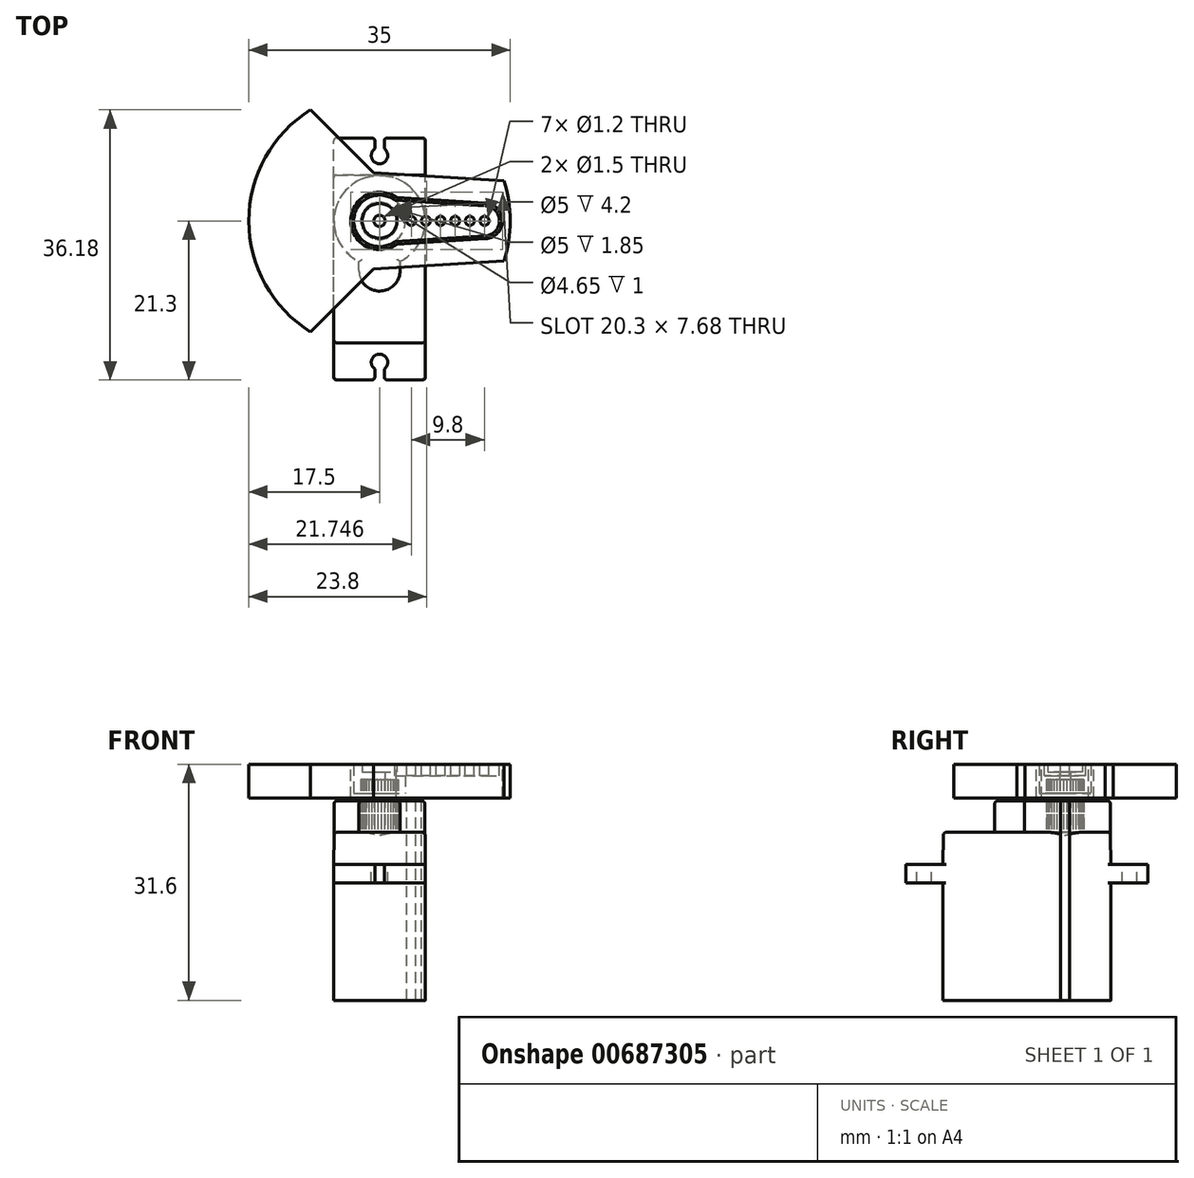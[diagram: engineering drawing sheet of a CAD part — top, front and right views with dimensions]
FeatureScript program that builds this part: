
annotation { "Feature Type Name" : "Feature", "Feature Type Description" : "" }
export const myFeature = defineFeature(function(context is Context, id is Id, definition is map)
    precondition{}
    {
        {
            var Q0;
            Q0=qCreatedBy(makeId("Top.planeOp"),FACE);
            var sketch = newSketch(context, id + "F0", { "sketchPlane" : qUnion([Q0])});
            skLineSegment(sketch, "E0.bottom", {"start": v(6.15, -11.25) * mm, "end": v(-6.15, -11.25) * mm});
            skLineSegment(sketch, "E0.top", {"start": v(6.15, 11.25) * mm, "end": v(-6.15, 11.25) * mm});
            skLineSegment(sketch, "E0.left", {"start": v(6.15, -11.25) * mm, "end": v(6.15, 11.25) * mm});
            skLineSegment(sketch, "E0.right", {"start": v(-6.15, -11.25) * mm, "end": v(-6.15, 11.25) * mm});
            skPoint(sketch, "E0.middle", {"position": v(0, 0) * mm});
            skSolve(sketch);
        }
        {
            var Q0;
            Q0=qSketchRegion(id+"F0",true);
            extrude(context, id + "F1", {"entities" : qUnion([Q0]), "depth" : (22.5 - 15.7) * mm, "hasDraft" : true, "draftAngle" : .5 * degree, "draftPullDirection" : true, "hasSecondDirection" : true, "secondDirectionOppositeDirection" : true, "secondDirectionDepth" : 15.7 * mm});
        }
        {
            var Q0;
            Q0=qCreatedBy(makeId("Top.planeOp"),FACE);
            var sketch = newSketch(context, id + "F2", { "sketchPlane" : qUnion([Q0])});
            skLineSegment(sketch, "E1.bottom", {"start": v(6.15, -16.2) * mm, "end": v(-6.15, -16.2) * mm});
            skLineSegment(sketch, "E1.top", {"start": v(6.15, 16.2) * mm, "end": v(-6.15, 16.2) * mm});
            skLineSegment(sketch, "E1.left", {"start": v(6.15, -16.2) * mm, "end": v(6.15, 16.2) * mm});
            skLineSegment(sketch, "E1.right", {"start": v(-6.15, -16.2) * mm, "end": v(-6.15, 16.2) * mm});
            skPoint(sketch, "E1.middle", {"position": v(0, 0) * mm});
            skSolve(sketch);
        }
        {
            var Q0;
            Q0=qSketchRegion(id+"F2",true);
            extrude(context, id + "F3", {"entities" : qUnion([Q0]), "operationType" : NewBodyOperationType.ADD, "depth" : 2.5 * mm, "hasDraft" : true, "draftAngle" : .5 * degree, "draftPullDirection" : true});
        }
        {
            var Q0;
            {var subQ0=sQuery(id+"F2.wireOp",EDGE,"E1.top");var subQ1=sQuery(id+"F2.wireOp",EDGE,"E1.right");var subQ2=sQuery(id+"F2.wireOp",EDGE,"E1.left");Q0=makeQuery(id+"F3.boolean.opBoolean","SPLIT",FACE,{"disambiguationData":[TD([makeQuery(id+"F1.opExtrude","SWEPT_FACE",FACE,{"disambiguationData":[OSD([sQuery(id+"F0.wireOp",EDGE,"E0.top")])]})])],"derivedFrom":makeQuery(id+"F3.opExtrude","CAP_FACE",FACE,{"disambiguationData":[OSD([sQuery(id+"F2.wireOp",EDGE,"E1.bottom"),subQ0,subQ2,subQ1])],"isStart":false})});}
            var sketch = newSketch(context, id + "F4", { "sketchPlane" : qUnion([Q0])});
            skArc(sketch, "E2", {"start": v(-0.63, 14.76) * mm, "mid": v(0, 12.75) * mm, "end": v(0.63, 14.76) * mm});
            skLineSegment(sketch, "E3", {"start": v(0, 0) * mm, "end": v(0, 13.85) * mm, "construction": true});
            skLineSegment(sketch, "E4", {"start": v(-0.63, 14.76) * mm, "end": v(-0.63, 16.2) * mm});
            skLineSegment(sketch, "E5", {"start": v(-0.62, 16.2) * mm, "end": v(0.62, 16.2) * mm});
            skLineSegment(sketch, "E6", {"start": v(0.62, 16.2) * mm, "end": v(0.62, 14.76) * mm});
            skLineSegment(sketch, "E7", {"start": v(0, 13.85) * mm, "end": v(0, 16.2) * mm, "construction": true});
            skLineSegment(sketch, "E8.MirrorCS", {"start": v(0.62, -16.2) * mm, "end": v(0.62, -14.76) * mm});
            skLineSegment(sketch, "E9.MirrorCS", {"start": v(-0.62, -16.2) * mm, "end": v(0.62, -16.2) * mm});
            skLineSegment(sketch, "E10.MirrorCS", {"start": v(-0.63, -14.76) * mm, "end": v(-0.63, -16.2) * mm});
            skArc(sketch, "E11.MirrorCS", {"start": v(-0.63, -14.76) * mm, "mid": v(0, -12.75) * mm, "end": v(0.63, -14.76) * mm});
            skSolve(sketch);
        }
        {
            var Q0;
            Q0=qSketchRegion(id+"F4",true);
            extrude(context, id + "F5", {"entities" : qUnion([Q0]), "operationType" : NewBodyOperationType.REMOVE, "endBound" : BoundingType.THROUGH_ALL, "oppositeDirection" : true, "depth" : 25 * mm});
        }
        {
            var Q0;
            Q0=makeQuery(id+"F1.*.split.splitOp","SPLIT",EDGE,{"derivedFrom":makeQuery(id+"F1.opExtrude","SWEPT_EDGE",EDGE,{"disambiguationData":[OSD([sQuery(id+"F0.wireOp",EDGE,"E0.bottom"),sQuery(id+"F0.wireOp",EDGE,"E0.left")])]})});
            var Q1;
            Q1=makeQuery(id+"F1.*.split.splitOp","SPLIT",EDGE,{"derivedFrom":makeQuery(id+"F1.opExtrude","SWEPT_EDGE",EDGE,{"disambiguationData":[OSD([sQuery(id+"F0.wireOp",EDGE,"E0.bottom"),sQuery(id+"F0.wireOp",EDGE,"E0.left")])]}),"isFromBackBody":true});
            var Q2;
            Q2=makeQuery(id+"F1.*.split.splitOp","SPLIT",EDGE,{"derivedFrom":makeQuery(id+"F1.opExtrude","SWEPT_EDGE",EDGE,{"disambiguationData":[OSD([sQuery(id+"F0.wireOp",EDGE,"E0.bottom"),sQuery(id+"F0.wireOp",EDGE,"E0.right")])]}),"isFromBackBody":true});
            var Q3;
            Q3=makeQuery(id+"F1.*.split.splitOp","SPLIT",EDGE,{"derivedFrom":makeQuery(id+"F1.opExtrude","SWEPT_EDGE",EDGE,{"disambiguationData":[OSD([sQuery(id+"F0.wireOp",EDGE,"E0.bottom"),sQuery(id+"F0.wireOp",EDGE,"E0.right")])]})});
            var Q4;
            Q4=makeQuery(id+"F1.opExtrude","CAP_FACE",FACE,{"disambiguationData":[OSD([sQuery(id+"F0.wireOp",EDGE,"E0.bottom"),sQuery(id+"F0.wireOp",EDGE,"E0.top"),sQuery(id+"F0.wireOp",EDGE,"E0.left"),sQuery(id+"F0.wireOp",EDGE,"E0.right")])],"isStart":false});
            var Q5;
            Q5=makeQuery(id+"F1.*.split.splitOp","SPLIT",EDGE,{"derivedFrom":makeQuery(id+"F1.opExtrude","SWEPT_EDGE",EDGE,{"disambiguationData":[OSD([sQuery(id+"F0.wireOp",EDGE,"E0.top"),sQuery(id+"F0.wireOp",EDGE,"E0.right")])]})});
            var Q6;
            Q6=makeQuery(id+"F1.*.split.splitOp","SPLIT",EDGE,{"derivedFrom":makeQuery(id+"F1.opExtrude","SWEPT_EDGE",EDGE,{"disambiguationData":[OSD([sQuery(id+"F0.wireOp",EDGE,"E0.top"),sQuery(id+"F0.wireOp",EDGE,"E0.right")])]}),"isFromBackBody":true});
            var Q7;
            Q7=makeQuery(id+"F1.*.split.splitOp","SPLIT",EDGE,{"derivedFrom":makeQuery(id+"F1.opExtrude","SWEPT_EDGE",EDGE,{"disambiguationData":[OSD([sQuery(id+"F0.wireOp",EDGE,"E0.top"),sQuery(id+"F0.wireOp",EDGE,"E0.left")])]}),"isFromBackBody":true});
            var Q8;
            Q8=makeQuery(id+"F1.*.split.splitOp","SPLIT",EDGE,{"derivedFrom":makeQuery(id+"F1.opExtrude","SWEPT_EDGE",EDGE,{"disambiguationData":[OSD([sQuery(id+"F0.wireOp",EDGE,"E0.top"),sQuery(id+"F0.wireOp",EDGE,"E0.left")])]})});
            var Q9;
            Q9=makeQuery(id+"F3.opExtrude","SWEPT_EDGE",EDGE,{"disambiguationData":[OSD([sQuery(id+"F2.wireOp",EDGE,"E1.top"),sQuery(id+"F2.wireOp",EDGE,"E1.left")])]});
            var Q10;
            Q10=makeQuery(id+"F5.boolean.opBoolean","INTERSECT",EDGE,{"derivedFrom":[makeQuery(id+"F3.opExtrude","SWEPT_FACE",FACE,{"disambiguationData":[OSD([sQuery(id+"F2.wireOp",EDGE,"E1.top")])]}),makeQuery(id+"F5.opExtrude","SWEPT_FACE",FACE,{"disambiguationData":[OSD([sQuery(id+"F4.wireOp",EDGE,"E6")])]})]});
            var Q11;
            Q11=makeQuery(id+"F5.boolean.opBoolean","INTERSECT",EDGE,{"derivedFrom":[makeQuery(id+"F3.opExtrude","SWEPT_FACE",FACE,{"disambiguationData":[OSD([sQuery(id+"F2.wireOp",EDGE,"E1.top")])]}),makeQuery(id+"F5.opExtrude","SWEPT_FACE",FACE,{"disambiguationData":[OSD([sQuery(id+"F4.wireOp",EDGE,"E4")])]})]});
            var Q12;
            Q12=makeQuery(id+"F3.opExtrude","SWEPT_EDGE",EDGE,{"disambiguationData":[OSD([sQuery(id+"F2.wireOp",EDGE,"E1.top"),sQuery(id+"F2.wireOp",EDGE,"E1.right")])]});
            var Q13;
            Q13=makeQuery(id+"F3.opExtrude","SWEPT_EDGE",EDGE,{"disambiguationData":[OSD([sQuery(id+"F2.wireOp",EDGE,"E1.bottom"),sQuery(id+"F2.wireOp",EDGE,"E1.right")])]});
            var Q14;
            Q14=makeQuery(id+"F5.boolean.opBoolean","INTERSECT",EDGE,{"derivedFrom":[makeQuery(id+"F3.opExtrude","SWEPT_FACE",FACE,{"disambiguationData":[OSD([sQuery(id+"F2.wireOp",EDGE,"E1.bottom")])]}),makeQuery(id+"F5.opExtrude","SWEPT_FACE",FACE,{"disambiguationData":[OSD([sQuery(id+"F4.wireOp",EDGE,"E10.MirrorCS")])]})]});
            var Q15;
            Q15=makeQuery(id+"F5.boolean.opBoolean","INTERSECT",EDGE,{"derivedFrom":[makeQuery(id+"F3.opExtrude","SWEPT_FACE",FACE,{"disambiguationData":[OSD([sQuery(id+"F2.wireOp",EDGE,"E1.bottom")])]}),makeQuery(id+"F5.opExtrude","SWEPT_FACE",FACE,{"disambiguationData":[OSD([sQuery(id+"F4.wireOp",EDGE,"E8.MirrorCS")])]})]});
            var Q16;
            Q16=makeQuery(id+"F3.opExtrude","SWEPT_EDGE",EDGE,{"disambiguationData":[OSD([sQuery(id+"F2.wireOp",EDGE,"E1.bottom"),sQuery(id+"F2.wireOp",EDGE,"E1.left")])]});
            fillet(context, id + "F6", {"entities" : qUnion([Q0, Q1, Q2, Q3, Q4, Q5, Q6, Q7, Q8, Q9, Q10, Q11, Q12, Q13, Q14, Q15, Q16]), "radius" : .4 * mm, "tangentPropagation" : true, "allowEdgeOverflow" : false});
        }
        {
            var Q0;
            Q0=makeQuery(id+"F1.opExtrude","CAP_FACE",FACE,{"disambiguationData":[OSD([sQuery(id+"F0.wireOp",EDGE,"E0.bottom"),sQuery(id+"F0.wireOp",EDGE,"E0.top"),sQuery(id+"F0.wireOp",EDGE,"E0.left"),sQuery(id+"F0.wireOp",EDGE,"E0.right")])],"isStart":false});
            var sketch = newSketch(context, id + "F7", { "sketchPlane" : qUnion([Q0])});
            skArc(sketch, "E12", {"start": v(2.75, -0.34) * mm, "mid": v(0, 11.2) * mm, "end": v(-2.75, -0.34) * mm});
            skLineSegment(sketch, "E13", {"start": v(-2.75, -0.34) * mm, "end": v(-2.75, -1.56) * mm});
            skLineSegment(sketch, "E14", {"start": v(2.75, -0.34) * mm, "end": v(2.75, -1.56) * mm});
            skArc(sketch, "E15", {"start": v(-2.75, -1.56) * mm, "mid": v(0, -4.3) * mm, "end": v(2.75, -1.56) * mm});
            skCircle(sketch, "E16", {"center": v(0, 5.1) * mm, "radius": 2.5 * mm});
            skSolve(sketch);
        }
        {
            var Q0;
            Q0=qSketchRegion(id+"F7",true);
            extrude(context, id + "F8", {"entities" : qUnion([Q0]), "operationType" : NewBodyOperationType.ADD, "depth" : 4.2 * mm, "hasSecondDirection" : true, "secondDirectionBound" : SecondDirectionBoundingType.UP_TO_NEXT, "secondDirectionOppositeDirection" : true, "secondDirectionDepth" : 25 * mm});
        }
        {
            var Q0;
            Q0=makeQuery(id+"F8.opExtrude","CAP_EDGE",EDGE,{"disambiguationData":[OSD([sQuery(id+"F7.wireOp",EDGE,"E12")])],"isStart":false});
            var Q1;
            Q1=makeQuery(id+"F8.opExtrude","CAP_EDGE",EDGE,{"disambiguationData":[OSD([sQuery(id+"F7.wireOp",EDGE,"E14")])],"isStart":false});
            var Q2;
            Q2=makeQuery(id+"F8.opExtrude","CAP_EDGE",EDGE,{"disambiguationData":[OSD([sQuery(id+"F7.wireOp",EDGE,"E15")])],"isStart":false});
            var Q3;
            Q3=makeQuery(id+"F8.opExtrude","CAP_EDGE",EDGE,{"disambiguationData":[OSD([sQuery(id+"F7.wireOp",EDGE,"E13")])],"isStart":false});
            fillet(context, id + "F9", {"entities" : qUnion([Q0, Q1, Q2, Q3]), "radius" : .4 * mm, "tangentPropagation" : true, "allowEdgeOverflow" : false});
        }
        {
            var Q0;
            Q0=makeQuery(id+"F8.opExtrude","CAP_FACE",FACE,{"disambiguationData":[OSD([sQuery(id+"F7.wireOp",EDGE,"E12"),sQuery(id+"F7.wireOp",EDGE,"E13"),sQuery(id+"F7.wireOp",EDGE,"E14"),sQuery(id+"F7.wireOp",EDGE,"E15"),sQuery(id+"F7.wireOp",EDGE,"E16")])],"isStart":false});
            var sketch = newSketch(context, id + "F10", { "sketchPlane" : qUnion([Q0])});
            skCircle(sketch, "E17", {"center": v(0, 5.1) * mm, "radius": 2.3 * mm, "construction": true});
            skLineSegment(sketch, "E18", {"start": v(-0.23, 7.39) * mm, "end": v(-0.06, 7.57) * mm});
            skLineSegment(sketch, "E19", {"start": v(0.23, 7.39) * mm, "end": v(0.06, 7.57) * mm});
            skArc(sketch, "E20", {"start": v(0.06, 7.57) * mm, "mid": v(0, 7.6) * mm, "end": v(-0.06, 7.57) * mm});
            skLineSegment(sketch, "E21", {"start": v(-0.23, 7.39) * mm, "end": v(0, 5.1) * mm, "construction": true});
            skLineSegment(sketch, "E22", {"start": v(0.23, 7.39) * mm, "end": v(0, 5.1) * mm, "construction": true});
            skLineSegment(sketch, "E23.1.0", {"start": v(-0.67, 7.3) * mm, "end": v(-0.54, 7.51) * mm});
            skArc(sketch, "E23.1.1", {"start": v(-0.42, 7.54) * mm, "mid": v(-0.49, 7.55) * mm, "end": v(-0.54, 7.51) * mm});
            skLineSegment(sketch, "E23.1.2", {"start": v(-0.23, 7.39) * mm, "end": v(-0.42, 7.54) * mm});
            skLineSegment(sketch, "E23.2.0", {"start": v(-1.08, 7.13) * mm, "end": v(-1, 7.36) * mm});
            skArc(sketch, "E23.2.1", {"start": v(-0.9, 7.4) * mm, "mid": v(-0.96, 7.4) * mm, "end": v(-1, 7.36) * mm});
            skLineSegment(sketch, "E23.2.2", {"start": v(-0.67, 7.3) * mm, "end": v(-0.9, 7.4) * mm});
            skLineSegment(sketch, "E23.3.0", {"start": v(-1.46, 6.88) * mm, "end": v(-1.42, 7.12) * mm});
            skArc(sketch, "E23.3.1", {"start": v(-1.32, 7.19) * mm, "mid": v(-1.39, 7.18) * mm, "end": v(-1.42, 7.12) * mm});
            skLineSegment(sketch, "E23.3.2", {"start": v(-1.08, 7.13) * mm, "end": v(-1.32, 7.19) * mm});
            skLineSegment(sketch, "E23.4.0", {"start": v(-1.78, 6.56) * mm, "end": v(-1.8, 6.8) * mm});
            skArc(sketch, "E23.4.1", {"start": v(-1.7, 6.9) * mm, "mid": v(-1.77, 6.87) * mm, "end": v(-1.8, 6.8) * mm});
            skLineSegment(sketch, "E23.4.2", {"start": v(-1.46, 6.88) * mm, "end": v(-1.7, 6.9) * mm});
            skLineSegment(sketch, "E23.5.0", {"start": v(-2.03, 6.18) * mm, "end": v(-2.09, 6.42) * mm});
            skArc(sketch, "E23.5.1", {"start": v(-2.02, 6.52) * mm, "mid": v(-2.08, 6.49) * mm, "end": v(-2.09, 6.42) * mm});
            skLineSegment(sketch, "E23.5.2", {"start": v(-1.78, 6.56) * mm, "end": v(-2.02, 6.52) * mm});
            skLineSegment(sketch, "E23.6.0", {"start": v(-2.2, 5.77) * mm, "end": v(-2.3, 6) * mm});
            skArc(sketch, "E23.6.1", {"start": v(-2.26, 6.1) * mm, "mid": v(-2.3, 6.06) * mm, "end": v(-2.3, 6) * mm});
            skLineSegment(sketch, "E23.6.2", {"start": v(-2.03, 6.18) * mm, "end": v(-2.26, 6.1) * mm});
            skLineSegment(sketch, "E23.7.0", {"start": v(-2.29, 5.33) * mm, "end": v(-2.44, 5.52) * mm});
            skArc(sketch, "E23.7.1", {"start": v(-2.41, 5.64) * mm, "mid": v(-2.45, 5.59) * mm, "end": v(-2.44, 5.52) * mm});
            skLineSegment(sketch, "E23.7.2", {"start": v(-2.2, 5.77) * mm, "end": v(-2.41, 5.64) * mm});
            skLineSegment(sketch, "E23.8.0", {"start": v(-2.29, 4.87) * mm, "end": v(-2.47, 5.04) * mm});
            skArc(sketch, "E23.8.1", {"start": v(-2.47, 5.16) * mm, "mid": v(-2.5, 5.1) * mm, "end": v(-2.47, 5.04) * mm});
            skLineSegment(sketch, "E23.8.2", {"start": v(-2.29, 5.33) * mm, "end": v(-2.47, 5.16) * mm});
            skLineSegment(sketch, "E23.9.0", {"start": v(-2.2, 4.43) * mm, "end": v(-2.41, 4.56) * mm});
            skArc(sketch, "E23.9.1", {"start": v(-2.44, 4.68) * mm, "mid": v(-2.45, 4.61) * mm, "end": v(-2.41, 4.56) * mm});
            skLineSegment(sketch, "E23.9.2", {"start": v(-2.29, 4.87) * mm, "end": v(-2.44, 4.68) * mm});
            skLineSegment(sketch, "E23.10.0", {"start": v(-2.03, 4.02) * mm, "end": v(-2.26, 4.1) * mm});
            skArc(sketch, "E23.10.1", {"start": v(-2.3, 4.2) * mm, "mid": v(-2.3, 4.14) * mm, "end": v(-2.26, 4.1) * mm});
            skLineSegment(sketch, "E23.10.2", {"start": v(-2.2, 4.43) * mm, "end": v(-2.3, 4.2) * mm});
            skLineSegment(sketch, "E23.11.0", {"start": v(-1.78, 3.64) * mm, "end": v(-2.02, 3.68) * mm});
            skArc(sketch, "E23.11.1", {"start": v(-2.09, 3.78) * mm, "mid": v(-2.08, 3.71) * mm, "end": v(-2.02, 3.68) * mm});
            skLineSegment(sketch, "E23.11.2", {"start": v(-2.03, 4.02) * mm, "end": v(-2.09, 3.78) * mm});
            skLineSegment(sketch, "E23.12.0", {"start": v(-1.46, 3.32) * mm, "end": v(-1.7, 3.3) * mm});
            skArc(sketch, "E23.12.1", {"start": v(-1.8, 3.4) * mm, "mid": v(-1.77, 3.33) * mm, "end": v(-1.7, 3.3) * mm});
            skLineSegment(sketch, "E23.12.2", {"start": v(-1.78, 3.64) * mm, "end": v(-1.8, 3.4) * mm});
            skLineSegment(sketch, "E23.13.0", {"start": v(-1.08, 3.07) * mm, "end": v(-1.32, 3.01) * mm});
            skArc(sketch, "E23.13.1", {"start": v(-1.42, 3.08) * mm, "mid": v(-1.39, 3.02) * mm, "end": v(-1.32, 3.01) * mm});
            skLineSegment(sketch, "E23.13.2", {"start": v(-1.46, 3.32) * mm, "end": v(-1.42, 3.08) * mm});
            skLineSegment(sketch, "E23.14.0", {"start": v(-0.67, 2.9) * mm, "end": v(-0.9, 2.8) * mm});
            skArc(sketch, "E23.14.1", {"start": v(-1, 2.84) * mm, "mid": v(-0.96, 2.8) * mm, "end": v(-0.9, 2.8) * mm});
            skLineSegment(sketch, "E23.14.2", {"start": v(-1.08, 3.07) * mm, "end": v(-1, 2.84) * mm});
            skLineSegment(sketch, "E23.15.0", {"start": v(-0.23, 2.81) * mm, "end": v(-0.42, 2.66) * mm});
            skArc(sketch, "E23.15.1", {"start": v(-0.54, 2.69) * mm, "mid": v(-0.49, 2.65) * mm, "end": v(-0.42, 2.66) * mm});
            skLineSegment(sketch, "E23.15.2", {"start": v(-0.67, 2.9) * mm, "end": v(-0.54, 2.69) * mm});
            skLineSegment(sketch, "E23.16.0", {"start": v(0.23, 2.81) * mm, "end": v(0.06, 2.63) * mm});
            skArc(sketch, "E23.16.1", {"start": v(-0.06, 2.63) * mm, "mid": v(0, 2.6) * mm, "end": v(0.06, 2.63) * mm});
            skLineSegment(sketch, "E23.16.2", {"start": v(-0.23, 2.81) * mm, "end": v(-0.06, 2.63) * mm});
            skLineSegment(sketch, "E23.17.0", {"start": v(0.67, 2.9) * mm, "end": v(0.54, 2.69) * mm});
            skArc(sketch, "E23.17.1", {"start": v(0.42, 2.66) * mm, "mid": v(0.49, 2.65) * mm, "end": v(0.54, 2.69) * mm});
            skLineSegment(sketch, "E23.17.2", {"start": v(0.23, 2.81) * mm, "end": v(0.42, 2.66) * mm});
            skLineSegment(sketch, "E23.18.0", {"start": v(1.08, 3.07) * mm, "end": v(1, 2.84) * mm});
            skArc(sketch, "E23.18.1", {"start": v(0.9, 2.8) * mm, "mid": v(0.96, 2.8) * mm, "end": v(1, 2.84) * mm});
            skLineSegment(sketch, "E23.18.2", {"start": v(0.67, 2.9) * mm, "end": v(0.9, 2.8) * mm});
            skLineSegment(sketch, "E23.19.0", {"start": v(1.46, 3.32) * mm, "end": v(1.42, 3.08) * mm});
            skArc(sketch, "E23.19.1", {"start": v(1.32, 3.01) * mm, "mid": v(1.39, 3.02) * mm, "end": v(1.42, 3.08) * mm});
            skLineSegment(sketch, "E23.19.2", {"start": v(1.08, 3.07) * mm, "end": v(1.32, 3.01) * mm});
            skLineSegment(sketch, "E23.20.0", {"start": v(1.78, 3.64) * mm, "end": v(1.8, 3.4) * mm});
            skArc(sketch, "E23.20.1", {"start": v(1.7, 3.3) * mm, "mid": v(1.77, 3.33) * mm, "end": v(1.8, 3.4) * mm});
            skLineSegment(sketch, "E23.20.2", {"start": v(1.46, 3.32) * mm, "end": v(1.7, 3.3) * mm});
            skLineSegment(sketch, "E23.21.0", {"start": v(2.03, 4.02) * mm, "end": v(2.09, 3.78) * mm});
            skArc(sketch, "E23.21.1", {"start": v(2.02, 3.68) * mm, "mid": v(2.08, 3.71) * mm, "end": v(2.09, 3.78) * mm});
            skLineSegment(sketch, "E23.21.2", {"start": v(1.78, 3.64) * mm, "end": v(2.02, 3.68) * mm});
            skLineSegment(sketch, "E23.22.0", {"start": v(2.2, 4.43) * mm, "end": v(2.3, 4.2) * mm});
            skArc(sketch, "E23.22.1", {"start": v(2.26, 4.1) * mm, "mid": v(2.3, 4.14) * mm, "end": v(2.3, 4.2) * mm});
            skLineSegment(sketch, "E23.22.2", {"start": v(2.03, 4.02) * mm, "end": v(2.26, 4.1) * mm});
            skLineSegment(sketch, "E23.23.0", {"start": v(2.29, 4.87) * mm, "end": v(2.44, 4.68) * mm});
            skArc(sketch, "E23.23.1", {"start": v(2.41, 4.56) * mm, "mid": v(2.45, 4.61) * mm, "end": v(2.44, 4.68) * mm});
            skLineSegment(sketch, "E23.23.2", {"start": v(2.2, 4.43) * mm, "end": v(2.41, 4.56) * mm});
            skLineSegment(sketch, "E23.24.0", {"start": v(2.29, 5.33) * mm, "end": v(2.47, 5.16) * mm});
            skArc(sketch, "E23.24.1", {"start": v(2.47, 5.04) * mm, "mid": v(2.5, 5.1) * mm, "end": v(2.47, 5.16) * mm});
            skLineSegment(sketch, "E23.24.2", {"start": v(2.29, 4.87) * mm, "end": v(2.47, 5.04) * mm});
            skLineSegment(sketch, "E23.25.0", {"start": v(2.2, 5.77) * mm, "end": v(2.41, 5.64) * mm});
            skArc(sketch, "E23.25.1", {"start": v(2.44, 5.52) * mm, "mid": v(2.45, 5.59) * mm, "end": v(2.41, 5.64) * mm});
            skLineSegment(sketch, "E23.25.2", {"start": v(2.29, 5.33) * mm, "end": v(2.44, 5.52) * mm});
            skLineSegment(sketch, "E23.26.0", {"start": v(2.03, 6.18) * mm, "end": v(2.26, 6.1) * mm});
            skArc(sketch, "E23.26.1", {"start": v(2.3, 6) * mm, "mid": v(2.3, 6.06) * mm, "end": v(2.26, 6.1) * mm});
            skLineSegment(sketch, "E23.26.2", {"start": v(2.2, 5.77) * mm, "end": v(2.3, 6) * mm});
            skLineSegment(sketch, "E23.27.0", {"start": v(1.78, 6.56) * mm, "end": v(2.02, 6.52) * mm});
            skArc(sketch, "E23.27.1", {"start": v(2.09, 6.42) * mm, "mid": v(2.08, 6.49) * mm, "end": v(2.02, 6.52) * mm});
            skLineSegment(sketch, "E23.27.2", {"start": v(2.03, 6.18) * mm, "end": v(2.09, 6.42) * mm});
            skLineSegment(sketch, "E23.28.0", {"start": v(1.46, 6.88) * mm, "end": v(1.7, 6.9) * mm});
            skArc(sketch, "E23.28.1", {"start": v(1.8, 6.8) * mm, "mid": v(1.77, 6.87) * mm, "end": v(1.7, 6.9) * mm});
            skLineSegment(sketch, "E23.28.2", {"start": v(1.78, 6.56) * mm, "end": v(1.8, 6.8) * mm});
            skLineSegment(sketch, "E23.29.0", {"start": v(1.08, 7.13) * mm, "end": v(1.32, 7.19) * mm});
            skArc(sketch, "E23.29.1", {"start": v(1.42, 7.12) * mm, "mid": v(1.39, 7.18) * mm, "end": v(1.32, 7.19) * mm});
            skLineSegment(sketch, "E23.29.2", {"start": v(1.46, 6.88) * mm, "end": v(1.42, 7.12) * mm});
            skLineSegment(sketch, "E23.30.0", {"start": v(0.67, 7.3) * mm, "end": v(0.9, 7.4) * mm});
            skArc(sketch, "E23.30.1", {"start": v(1, 7.36) * mm, "mid": v(0.96, 7.4) * mm, "end": v(0.9, 7.4) * mm});
            skLineSegment(sketch, "E23.30.2", {"start": v(1.08, 7.13) * mm, "end": v(1, 7.36) * mm});
            skLineSegment(sketch, "E23.31.0", {"start": v(0.23, 7.39) * mm, "end": v(0.42, 7.54) * mm});
            skArc(sketch, "E23.31.1", {"start": v(0.54, 7.51) * mm, "mid": v(0.49, 7.55) * mm, "end": v(0.42, 7.54) * mm});
            skLineSegment(sketch, "E23.31.2", {"start": v(0.67, 7.3) * mm, "end": v(0.54, 7.51) * mm});
            skCircle(sketch, "E24", {"center": v(0, 5.1) * mm, "radius": 0.75 * mm});
            skSolve(sketch);
        }
        {
            var Q0;
            Q0=qSketchRegion(id+"F10",true);
            extrude(context, id + "F11", {"entities" : qUnion([Q0]), "depth" : 2.85 * mm, "hasSecondDirection" : true, "secondDirectionBound" : SecondDirectionBoundingType.UP_TO_NEXT, "secondDirectionOppositeDirection" : true, "secondDirectionDepth" : 25 * mm, "offsetDistance" : 25 * mm});
        }
        {
            var Q0;
            Q0=qCreatedBy(makeId("Right.planeOp"),FACE);
            var sketch = newSketch(context, id + "F12", { "sketchPlane" : qUnion([Q0])});
            skLineSegment(sketch, "E25.0", {"start": v(4.35, 13.85) * mm, "end": v(5.85, 13.85) * mm, "construction": true});
            skLineSegment(sketch, "E26", {"start": v(5.85, 13.85) * mm, "end": v(7.6, 13.85) * mm});
            skLineSegment(sketch, "E27", {"start": v(7.6, 13.85) * mm, "end": v(7.6, 12) * mm});
            skLineSegment(sketch, "E28", {"start": v(7.6, 12) * mm, "end": v(8.55, 12) * mm});
            skLineSegment(sketch, "E29", {"start": v(8.55, 12) * mm, "end": v(8.55, 15.9) * mm});
            skLineSegment(sketch, "E30", {"start": v(8.55, 15.9) * mm, "end": v(7.43, 15.9) * mm});
            skLineSegment(sketch, "E31", {"start": v(7.43, 15.9) * mm, "end": v(7.43, 14.9) * mm});
            skLineSegment(sketch, "E32", {"start": v(7.43, 14.9) * mm, "end": v(5.85, 14.9) * mm});
            skLineSegment(sketch, "E33", {"start": v(5.85, 14.9) * mm, "end": v(5.85, 13.85) * mm});
            skLineSegment(sketch, "E34", {"start": v(5.1, 13.85) * mm, "end": v(5.1, 16.3) * mm, "construction": true});
            skLineSegment(sketch, "E35.0", {"start": v(2.6, 11) * mm, "end": v(7.6, 11) * mm, "construction": true});
            skSolve(sketch);
        }
        {
            var Q0;
            Q0=qSketchRegion(id+"F12",true);
            var Q1;
            Q1 = qSketchRegion(id + "F19", true);
            var Q2;
            Q2=sQuery(id+"F12.wireOp",EDGE,"E34");
            revolve(context, id + "F13", {"entities" : qUnion([Q0, Q1]), "axis" : qUnion([Q2]), "revolveType" : RevolveType.FULL, "surfaceOperationType" : NewSurfaceOperationType.NEW});
        }
        {
            var Q0;
            Q0=makeQuery(id+"F13.opRevolve","SWEPT_FACE",FACE,{"disambiguationData":[OSD([sQuery(id+"F12.wireOp",EDGE,"E30")])]});
            var sketch = newSketch(context, id + "F14", { "sketchPlane" : qUnion([Q0])});
            skLineSegment(sketch, "E36", {"start": v(2.08, 2.35) * mm, "end": v(14.17, 3.1) * mm});
            skLineSegment(sketch, "E37", {"start": v(2.08, 7.85) * mm, "end": v(14.17, 7.1) * mm});
            skLineSegment(sketch, "E38", {"start": v(0, 5.1) * mm, "end": v(14.05, 5.1) * mm, "construction": true});
            skArc(sketch, "E39", {"start": v(14.17, 3.1) * mm, "mid": v(16.05, 5.1) * mm, "end": v(14.17, 7.1) * mm});
            skArc(sketch, "E40.0", {"start": v(2.08, 2.35) * mm, "mid": v(3.45, 5.1) * mm, "end": v(2.08, 7.85) * mm});
            skSolve(sketch);
        }
        {
            var Q0;
            Q0=qSketchRegion(id+"F14",true);
            extrude(context, id + "F15", {"entities" : qUnion([Q0]), "operationType" : NewBodyOperationType.ADD, "oppositeDirection" : true, "depth" : 1.5 * mm, "offsetDistance" : 25 * mm});
        }
        {
            var Q0;
            Q0=makeQuery(id+"F15.boolean.opBoolean","MERGE",FACE,{"derivedFrom":[makeQuery(id+"F13.opRevolve","SWEPT_FACE",FACE,{"disambiguationData":[OSD([sQuery(id+"F12.wireOp",EDGE,"E30")])]}),makeQuery(id+"F15.opExtrude","CAP_FACE",FACE,{"disambiguationData":[OSD([sQuery(id+"F14.wireOp",EDGE,"E36"),sQuery(id+"F14.wireOp",EDGE,"E37"),sQuery(id+"F14.wireOp",EDGE,"E39"),sQuery(id+"F14.wireOp",EDGE,"E40.0")])],"isStart":true})]});
            var sketch = newSketch(context, id + "F16", { "sketchPlane" : qUnion([Q0])});
            skCircle(sketch, "E41", {"center": v(14.05, 5.1) * mm, "radius": 0.6 * mm});
            skCircle(sketch, "E42.1.0.0", {"center": v(12.09, 5.1) * mm, "radius": 0.6 * mm});
            skCircle(sketch, "E42.2.0.0", {"center": v(10.13, 5.1) * mm, "radius": 0.6 * mm});
            skCircle(sketch, "E42.3.0.0", {"center": v(8.17, 5.1) * mm, "radius": 0.6 * mm});
            skCircle(sketch, "E42.4.0.0", {"center": v(6.2, 5.1) * mm, "radius": 0.6 * mm});
            skCircle(sketch, "E42.5.0.0", {"center": v(4.25, 5.1) * mm, "radius": 0.6 * mm});
            skLineSegment(sketch, "E42.direction1", {"start": v(14.05, 5.1) * mm, "end": v(12.09, 5.1) * mm, "construction": true});
            skSolve(sketch);
        }
        {
            var Q0;
            Q0=qSketchRegion(id+"F16",true);
            extrude(context, id + "F17", {"entities" : qUnion([Q0]), "operationType" : NewBodyOperationType.REMOVE, "endBound" : BoundingType.THROUGH_ALL, "oppositeDirection" : true, "depth" : 25 * mm, "offsetDistance" : 25 * mm});
        }
        {
            var Q0;
            Q0=makeQuery(id+"F15.boolean.opBoolean","MERGE",FACE,{"derivedFrom":[makeQuery(id+"F13.opRevolve","SWEPT_FACE",FACE,{"disambiguationData":[OSD([sQuery(id+"F12.wireOp",EDGE,"E30")])]}),makeQuery(id+"F15.opExtrude","CAP_FACE",FACE,{"disambiguationData":[OSD([sQuery(id+"F14.wireOp",EDGE,"E36"),sQuery(id+"F14.wireOp",EDGE,"E37"),sQuery(id+"F14.wireOp",EDGE,"E39"),sQuery(id+"F14.wireOp",EDGE,"E40.0")])],"isStart":true})]});
            var sketch = newSketch(context, id + "F18", { "sketchPlane" : qUnion([Q0])});
            skArc(sketch, "E43.0", {"start": v(2.22, 8.24) * mm, "mid": v(-3.85, 5.1) * mm, "end": v(2.22, 1.96) * mm});
            skLineSegment(sketch, "E43.1", {"start": v(14.2, 7.5) * mm, "end": v(2.22, 8.24) * mm});
            skArc(sketch, "E43.2", {"start": v(14.2, 2.7) * mm, "mid": v(16.45, 5.1) * mm, "end": v(14.2, 7.5) * mm});
            skLineSegment(sketch, "E43.3", {"start": v(2.22, 1.96) * mm, "end": v(14.2, 2.7) * mm});
            skSolve(sketch);
        }
        {
            var Q0;
            Q0=makeQuery(id+"F18.imprint","IMPRINT",FACE,{"disambiguationData":[TD([[makeQuery(id+"F18.imprint","IMPRINT",EDGE,{"derivedFrom":sQuery(id+"F18.wireOp",EDGE,"E43.0")}),1.0]])]});
            var sketch = newSketch(context, id + "F19", { "sketchPlane" : qUnion([Q0])});
            skCircle(sketch, "E44", {"center": v(0, 5.1) * mm, "radius": 17.5 * mm});
            skLineSegment(sketch, "E45", {"start": v(0, 5.1) * mm, "end": v(-14.14, -9.04) * mm});
            skLineSegment(sketch, "E46", {"start": v(0, 5.1) * mm, "end": v(-20.07, 5.1) * mm});
            skLineSegment(sketch, "E47.MirrorCS", {"start": v(0, 5.1) * mm, "end": v(-14.14, 19.24) * mm});
            skCircle(sketch, "E48", {"center": v(-14, 5.1) * mm, "radius": 2 * mm});
            skCircle(sketch, "E49", {"center": v(0, 5.1) * mm, "radius": 14 * mm});
            skCircle(sketch, "E50.1.0", {"center": v(-12.93, 10.46) * mm, "radius": 2 * mm});
            skCircle(sketch, "E50.2.0", {"center": v(-9.9, 15) * mm, "radius": 2 * mm});
            skLineSegment(sketch, "E50.anchor1", {"start": v(0, 5.1) * mm, "end": v(-14, 5.1) * mm, "construction": true});
            skLineSegment(sketch, "E50.anchor2", {"start": v(0, 5.1) * mm, "end": v(-9.9, 15) * mm, "construction": true});
            skCircle(sketch, "E51.MirrorC", {"center": v(-12.93, -0.26) * mm, "radius": 2 * mm});
            skCircle(sketch, "E52.MirrorC", {"center": v(-9.9, -4.8) * mm, "radius": 2 * mm});
            skLineSegment(sketch, "E53.0", {"start": v(5.66, 5.1) * mm, "end": v(-11.31, 22.07) * mm});
            skLineSegment(sketch, "E53.1", {"start": v(5.66, 5.1) * mm, "end": v(-11.31, -11.87) * mm});
            skLineSegment(sketch, "E54", {"start": v(0, 5.1) * mm, "end": v(-12.93, -0.26) * mm});
            skLineSegment(sketch, "E55", {"start": v(0, 5.1) * mm, "end": v(-12.93, 10.46) * mm});
            skLineSegment(sketch, "E56", {"start": v(-12.04, 12.25) * mm, "end": v(19.23, 10.3) * mm});
            skLineSegment(sketch, "E57.MirrorCS", {"start": v(-12.04, -2.05) * mm, "end": v(19.23, -0.1) * mm});
            skSolve(sketch);
        }
        {
            var Q0;
            {var subQ5=sQuery(id+"F19.wireOp",EDGE,"E53.0");var subQ7=sQuery(id+"F19.wireOp",EDGE,"E44");var subQ8=makeQuery(id+"F19.imprint","INTERSECT",VERTEX,{"derivedFrom":[subQ7,subQ5]});Q0=makeQuery(id+"F19.imprint","IMPRINT",FACE,{"disambiguationData":[TD([[makeQuery(id+"F19.imprint","IMPRINT",EDGE,{"disambiguationData":[TD([[subQ8,-1.0]])],"derivedFrom":subQ7}),1.0]])]});}
            var Q1;
            {var subQ3=sQuery(id+"F19.wireOp",EDGE,"E56");var subQ6=sQuery(id+"F19.wireOp",EDGE,"E47.MirrorCS");var subQ9=makeQuery(id+"F19.imprint","INTERSECT",VERTEX,{"derivedFrom":[subQ6,subQ3]});Q1=makeQuery(id+"F19.imprint","IMPRINT",FACE,{"disambiguationData":[TD([[makeQuery(id+"F19.imprint","IMPRINT",EDGE,{"disambiguationData":[TD([[subQ9,-1.0]])],"derivedFrom":subQ6}),-1.0]])]});}
            var Q2;
            {var subQ3=sQuery(id+"F19.wireOp",EDGE,"E47.MirrorCS");var subQ5=sQuery(id+"F19.wireOp",EDGE,"E56");var subQ9=makeQuery(id+"F19.imprint","INTERSECT",VERTEX,{"derivedFrom":[subQ3,subQ5]});Q2=makeQuery(id+"F19.imprint","IMPRINT",FACE,{"disambiguationData":[TD([[makeQuery(id+"F19.imprint","IMPRINT",EDGE,{"disambiguationData":[TD([[subQ9,1.0]])],"derivedFrom":subQ3}),-1.0]])]});}
            var Q3;
            {var subQ0=sQuery(id+"F19.wireOp",EDGE,"E56");var subQ1=sQuery(id+"F19.wireOp",EDGE,"E49");var subQ2=makeQuery(id+"F19.imprint","INTERSECT",VERTEX,{"derivedFrom":[subQ1,subQ0]});Q3=makeQuery(id+"F19.imprint","IMPRINT",FACE,{"disambiguationData":[TD([[makeQuery(id+"F19.imprint","IMPRINT",EDGE,{"disambiguationData":[TD([[subQ2,1.0]])],"derivedFrom":subQ1}),1.0]])]});}
            var Q4;
            {var subQ12=makeQuery(id+"F18.imprint","IMPRINT",EDGE,{"derivedFrom":sQuery(id+"F18.wireOp",EDGE,"E43.2")});Q4=makeQuery(id+"F19.imprint","IMPRINT",FACE,{"disambiguationData":[TD([[makeQuery(id+"F19.imprint","IMPRINT",EDGE,{"derivedFrom":subQ12}),-1.0]])]});}
            var Q5;
            {var subQ0=sQuery(id+"F19.wireOp",EDGE,"E57.MirrorCS");var subQ1=sQuery(id+"F19.wireOp",EDGE,"E49");var subQ2=makeQuery(id+"F19.imprint","INTERSECT",VERTEX,{"derivedFrom":[subQ1,subQ0]});Q5=makeQuery(id+"F19.imprint","IMPRINT",FACE,{"disambiguationData":[TD([[makeQuery(id+"F19.imprint","IMPRINT",EDGE,{"disambiguationData":[TD([[subQ2,-1.0]])],"derivedFrom":subQ1}),1.0]])]});}
            var Q6;
            {var subQ3=sQuery(id+"F19.wireOp",EDGE,"E45");var subQ5=sQuery(id+"F19.wireOp",EDGE,"E57.MirrorCS");var subQ9=makeQuery(id+"F19.imprint","INTERSECT",VERTEX,{"derivedFrom":[subQ3,subQ5]});Q6=makeQuery(id+"F19.imprint","IMPRINT",FACE,{"disambiguationData":[TD([[makeQuery(id+"F19.imprint","IMPRINT",EDGE,{"disambiguationData":[TD([[subQ9,1.0]])],"derivedFrom":subQ3}),1.0]])]});}
            var Q7;
            {var subQ0=sQuery(id+"F19.wireOp",EDGE,"E57.MirrorCS");var subQ3=sQuery(id+"F19.wireOp",EDGE,"E45");var subQ4=makeQuery(id+"F19.imprint","INTERSECT",VERTEX,{"derivedFrom":[subQ3,subQ0]});Q7=makeQuery(id+"F19.imprint","IMPRINT",FACE,{"disambiguationData":[TD([[makeQuery(id+"F19.imprint","IMPRINT",EDGE,{"disambiguationData":[TD([[subQ4,1.0]])],"derivedFrom":subQ3}),-1.0]])]});}
            var Q8;
            {var subQ0=sQuery(id+"F19.wireOp",EDGE,"E56");var subQ3=sQuery(id+"F19.wireOp",EDGE,"E47.MirrorCS");var subQ4=makeQuery(id+"F19.imprint","INTERSECT",VERTEX,{"derivedFrom":[subQ3,subQ0]});Q8=makeQuery(id+"F19.imprint","IMPRINT",FACE,{"disambiguationData":[TD([[makeQuery(id+"F19.imprint","IMPRINT",EDGE,{"disambiguationData":[TD([[subQ4,1.0]])],"derivedFrom":subQ3}),1.0]])]});}
            var Q9;
            {var subQ1=sQuery(id+"F19.wireOp",EDGE,"E48");var subQ9=sQuery(id+"F19.wireOp",EDGE,"E46");var subQ10=makeQuery(id+"F19.imprint","INTERSECT",VERTEX,{"disambiguationData":[OD(0.0)],"derivedFrom":[subQ9,subQ1]});Q9=makeQuery(id+"F19.imprint","IMPRINT",FACE,{"disambiguationData":[TD([[makeQuery(id+"F19.imprint","IMPRINT",EDGE,{"disambiguationData":[TD([[subQ10,1.0]])],"derivedFrom":subQ9}),-1.0]])]});}
            var Q10;
            {var subQ5=sQuery(id+"F19.wireOp",EDGE,"E48");var subQ6=sQuery(id+"F19.wireOp",EDGE,"E46");var subQ7=makeQuery(id+"F19.imprint","INTERSECT",VERTEX,{"disambiguationData":[OD(0.0)],"derivedFrom":[subQ6,subQ5]});Q10=makeQuery(id+"F19.imprint","IMPRINT",FACE,{"disambiguationData":[TD([[makeQuery(id+"F19.imprint","IMPRINT",EDGE,{"disambiguationData":[TD([[subQ7,1.0]])],"derivedFrom":subQ6}),1.0]])]});}
            var Q11;
            {var subQ3=sQuery(id+"F19.wireOp",EDGE,"E57.MirrorCS");var subQ5=sQuery(id+"F19.wireOp",EDGE,"E45");var subQ6=makeQuery(id+"F19.imprint","INTERSECT",VERTEX,{"derivedFrom":[subQ5,subQ3]});Q11=makeQuery(id+"F19.imprint","IMPRINT",FACE,{"disambiguationData":[TD([[makeQuery(id+"F19.imprint","IMPRINT",EDGE,{"disambiguationData":[TD([[subQ6,-1.0]])],"derivedFrom":subQ5}),1.0]])]});}
            var Q12;
            {var subQ0=sQuery(id+"F19.wireOp",EDGE,"E57.MirrorCS");var subQ1=sQuery(id+"F19.wireOp",EDGE,"E45");var subQ2=makeQuery(id+"F19.imprint","INTERSECT",VERTEX,{"derivedFrom":[subQ1,subQ0]});Q12=makeQuery(id+"F19.imprint","IMPRINT",FACE,{"disambiguationData":[TD([[makeQuery(id+"F19.imprint","IMPRINT",EDGE,{"disambiguationData":[TD([[subQ2,-1.0]])],"derivedFrom":subQ1}),-1.0]])]});}
            var Q13;
            {var subQ0=sQuery(id+"F19.wireOp",EDGE,"E56");var subQ1=sQuery(id+"F19.wireOp",EDGE,"E47.MirrorCS");var subQ2=makeQuery(id+"F19.imprint","INTERSECT",VERTEX,{"derivedFrom":[subQ1,subQ0]});Q13=makeQuery(id+"F19.imprint","IMPRINT",FACE,{"disambiguationData":[TD([[makeQuery(id+"F19.imprint","IMPRINT",EDGE,{"disambiguationData":[TD([[subQ2,-1.0]])],"derivedFrom":subQ1}),1.0]])]});}
            var Q14;
            {var subQ5=sQuery(id+"F19.wireOp",EDGE,"E47.MirrorCS");var subQ6=sQuery(id+"F19.wireOp",EDGE,"E44");var subQ7=makeQuery(id+"F19.imprint","INTERSECT",VERTEX,{"derivedFrom":[subQ6,subQ5]});Q14=makeQuery(id+"F19.imprint","IMPRINT",FACE,{"disambiguationData":[TD([[makeQuery(id+"F19.imprint","IMPRINT",EDGE,{"disambiguationData":[TD([[subQ7,-1.0]])],"derivedFrom":subQ6}),1.0]])]});}
            var Q15;
            {var subQ1=sQuery(id+"F19.wireOp",EDGE,"E46");var subQ8=sQuery(id+"F19.wireOp",EDGE,"E44");var subQ9=makeQuery(id+"F19.imprint","INTERSECT",VERTEX,{"derivedFrom":[subQ8,subQ1]});Q15=makeQuery(id+"F19.imprint","IMPRINT",FACE,{"disambiguationData":[TD([[makeQuery(id+"F19.imprint","IMPRINT",EDGE,{"disambiguationData":[TD([[subQ9,-1.0]])],"derivedFrom":subQ8}),1.0]])]});}
            var Q16;
            {var subQ1=sQuery(id+"F19.wireOp",EDGE,"E45");var subQ5=sQuery(id+"F19.wireOp",EDGE,"E44");var subQ6=makeQuery(id+"F19.imprint","INTERSECT",VERTEX,{"derivedFrom":[subQ5,subQ1]});Q16=makeQuery(id+"F19.imprint","IMPRINT",FACE,{"disambiguationData":[TD([[makeQuery(id+"F19.imprint","IMPRINT",EDGE,{"disambiguationData":[TD([[subQ6,-1.0]])],"derivedFrom":subQ5}),1.0]])]});}
            var Q17;
            {var subQ0=sQuery(id+"F19.wireOp",EDGE,"E49");var subQ1=sQuery(id+"F19.wireOp",EDGE,"E47.MirrorCS");var subQ2=makeQuery(id+"F19.imprint","INTERSECT",VERTEX,{"derivedFrom":[subQ1,subQ0]});Q17=makeQuery(id+"F19.imprint","IMPRINT",FACE,{"disambiguationData":[TD([[makeQuery(id+"F19.imprint","IMPRINT",EDGE,{"disambiguationData":[TD([[subQ2,-1.0]])],"derivedFrom":subQ1}),-1.0]])]});}
            var Q18;
            {var subQ0=sQuery(id+"F19.wireOp",EDGE,"E49");var subQ1=sQuery(id+"F19.wireOp",EDGE,"E47.MirrorCS");var subQ2=makeQuery(id+"F19.imprint","INTERSECT",VERTEX,{"derivedFrom":[subQ1,subQ0]});Q18=makeQuery(id+"F19.imprint","IMPRINT",FACE,{"disambiguationData":[TD([[makeQuery(id+"F19.imprint","IMPRINT",EDGE,{"disambiguationData":[TD([[subQ2,-1.0]])],"derivedFrom":subQ1}),1.0]])]});}
            var Q19;
            {var subQ0=sQuery(id+"F19.wireOp",EDGE,"E50.2.0");var subQ1=sQuery(id+"F19.wireOp",EDGE,"E47.MirrorCS");var subQ2=makeQuery(id+"F19.imprint","INTERSECT",VERTEX,{"disambiguationData":[OD(0.0)],"derivedFrom":[subQ1,subQ0]});Q19=makeQuery(id+"F19.imprint","IMPRINT",FACE,{"disambiguationData":[TD([[makeQuery(id+"F19.imprint","IMPRINT",EDGE,{"disambiguationData":[TD([[subQ2,-1.0]])],"derivedFrom":subQ1}),1.0]])]});}
            var Q20;
            {var subQ0=sQuery(id+"F19.wireOp",EDGE,"E50.2.0");var subQ1=sQuery(id+"F19.wireOp",EDGE,"E47.MirrorCS");var subQ2=makeQuery(id+"F19.imprint","INTERSECT",VERTEX,{"disambiguationData":[OD(0.0)],"derivedFrom":[subQ1,subQ0]});Q20=makeQuery(id+"F19.imprint","IMPRINT",FACE,{"disambiguationData":[TD([[makeQuery(id+"F19.imprint","IMPRINT",EDGE,{"disambiguationData":[TD([[subQ2,-1.0]])],"derivedFrom":subQ1}),-1.0]])]});}
            var Q21;
            {var subQ0=sQuery(id+"F19.wireOp",EDGE,"E49");var subQ1=makeQuery(id+"F19.imprint","INTERSECT",VERTEX,{"derivedFrom":[subQ0,sQuery(id+"F19.wireOp",EDGE,"E55")]});Q21=makeQuery(id+"F19.imprint","IMPRINT",FACE,{"disambiguationData":[TD([[makeQuery(id+"F19.imprint","IMPRINT",EDGE,{"disambiguationData":[TD([[subQ1,-1.0]])],"derivedFrom":subQ0}),-1.0]])]});}
            var Q22;
            {var subQ0=sQuery(id+"F19.wireOp",EDGE,"E55");var subQ1=sQuery(id+"F19.wireOp",EDGE,"E49");var subQ2=makeQuery(id+"F19.imprint","INTERSECT",VERTEX,{"derivedFrom":[subQ1,subQ0]});Q22=makeQuery(id+"F19.imprint","IMPRINT",FACE,{"disambiguationData":[TD([[makeQuery(id+"F19.imprint","IMPRINT",EDGE,{"disambiguationData":[TD([[subQ2,1.0]])],"derivedFrom":subQ0}),-1.0]])]});}
            var Q23;
            {var subQ0=sQuery(id+"F19.wireOp",EDGE,"E55");var subQ1=sQuery(id+"F19.wireOp",EDGE,"E49");var subQ2=makeQuery(id+"F19.imprint","INTERSECT",VERTEX,{"derivedFrom":[subQ1,subQ0]});Q23=makeQuery(id+"F19.imprint","IMPRINT",FACE,{"disambiguationData":[TD([[makeQuery(id+"F19.imprint","IMPRINT",EDGE,{"disambiguationData":[TD([[subQ2,-1.0]])],"derivedFrom":subQ1}),1.0]])]});}
            var Q24;
            {var subQ0=sQuery(id+"F19.wireOp",EDGE,"E49");var subQ1=sQuery(id+"F19.wireOp",EDGE,"E46");var subQ2=makeQuery(id+"F19.imprint","INTERSECT",VERTEX,{"derivedFrom":[subQ1,subQ0]});Q24=makeQuery(id+"F19.imprint","IMPRINT",FACE,{"disambiguationData":[TD([[makeQuery(id+"F19.imprint","IMPRINT",EDGE,{"disambiguationData":[TD([[subQ2,-1.0]])],"derivedFrom":subQ1}),-1.0]])]});}
            var Q25;
            {var subQ0=sQuery(id+"F19.wireOp",EDGE,"E48");var subQ1=sQuery(id+"F19.wireOp",EDGE,"E46");var subQ2=makeQuery(id+"F19.imprint","INTERSECT",VERTEX,{"disambiguationData":[OD(0.0)],"derivedFrom":[subQ1,subQ0]});Q25=makeQuery(id+"F19.imprint","IMPRINT",FACE,{"disambiguationData":[TD([[makeQuery(id+"F19.imprint","IMPRINT",EDGE,{"disambiguationData":[TD([[subQ2,-1.0]])],"derivedFrom":subQ1}),-1.0]])]});}
            var Q26;
            {var subQ0=sQuery(id+"F19.wireOp",EDGE,"E48");var subQ1=sQuery(id+"F19.wireOp",EDGE,"E46");var subQ2=makeQuery(id+"F19.imprint","INTERSECT",VERTEX,{"disambiguationData":[OD(0.0)],"derivedFrom":[subQ1,subQ0]});Q26=makeQuery(id+"F19.imprint","IMPRINT",FACE,{"disambiguationData":[TD([[makeQuery(id+"F19.imprint","IMPRINT",EDGE,{"disambiguationData":[TD([[subQ2,-1.0]])],"derivedFrom":subQ1}),1.0]])]});}
            var Q27;
            {var subQ0=sQuery(id+"F19.wireOp",EDGE,"E49");var subQ1=sQuery(id+"F19.wireOp",EDGE,"E46");var subQ2=makeQuery(id+"F19.imprint","INTERSECT",VERTEX,{"derivedFrom":[subQ1,subQ0]});Q27=makeQuery(id+"F19.imprint","IMPRINT",FACE,{"disambiguationData":[TD([[makeQuery(id+"F19.imprint","IMPRINT",EDGE,{"disambiguationData":[TD([[subQ2,-1.0]])],"derivedFrom":subQ1}),1.0]])]});}
            var Q28;
            {var subQ0=sQuery(id+"F19.wireOp",EDGE,"E49");var subQ1=makeQuery(id+"F19.imprint","INTERSECT",VERTEX,{"derivedFrom":[subQ0,sQuery(id+"F19.wireOp",EDGE,"E54")]});Q28=makeQuery(id+"F19.imprint","IMPRINT",FACE,{"disambiguationData":[TD([[makeQuery(id+"F19.imprint","IMPRINT",EDGE,{"disambiguationData":[TD([[subQ1,1.0]])],"derivedFrom":subQ0}),-1.0]])]});}
            var Q29;
            {var subQ0=sQuery(id+"F19.wireOp",EDGE,"E54");var subQ1=sQuery(id+"F19.wireOp",EDGE,"E49");var subQ2=makeQuery(id+"F19.imprint","INTERSECT",VERTEX,{"derivedFrom":[subQ1,subQ0]});Q29=makeQuery(id+"F19.imprint","IMPRINT",FACE,{"disambiguationData":[TD([[makeQuery(id+"F19.imprint","IMPRINT",EDGE,{"disambiguationData":[TD([[subQ2,1.0]])],"derivedFrom":subQ1}),1.0]])]});}
            var Q30;
            {var subQ0=sQuery(id+"F19.wireOp",EDGE,"E54");var subQ1=sQuery(id+"F19.wireOp",EDGE,"E49");var subQ2=makeQuery(id+"F19.imprint","INTERSECT",VERTEX,{"derivedFrom":[subQ1,subQ0]});Q30=makeQuery(id+"F19.imprint","IMPRINT",FACE,{"disambiguationData":[TD([[makeQuery(id+"F19.imprint","IMPRINT",EDGE,{"disambiguationData":[TD([[subQ2,1.0]])],"derivedFrom":subQ0}),1.0]])]});}
            var Q31;
            {var subQ0=sQuery(id+"F19.wireOp",EDGE,"E49");var subQ1=sQuery(id+"F19.wireOp",EDGE,"E45");var subQ2=makeQuery(id+"F19.imprint","INTERSECT",VERTEX,{"derivedFrom":[subQ1,subQ0]});Q31=makeQuery(id+"F19.imprint","IMPRINT",FACE,{"disambiguationData":[TD([[makeQuery(id+"F19.imprint","IMPRINT",EDGE,{"disambiguationData":[TD([[subQ2,-1.0]])],"derivedFrom":subQ1}),-1.0]])]});}
            var Q32;
            {var subQ0=sQuery(id+"F19.wireOp",EDGE,"E49");var subQ1=sQuery(id+"F19.wireOp",EDGE,"E45");var subQ2=makeQuery(id+"F19.imprint","INTERSECT",VERTEX,{"derivedFrom":[subQ1,subQ0]});Q32=makeQuery(id+"F19.imprint","IMPRINT",FACE,{"disambiguationData":[TD([[makeQuery(id+"F19.imprint","IMPRINT",EDGE,{"disambiguationData":[TD([[subQ2,-1.0]])],"derivedFrom":subQ1}),1.0]])]});}
            var Q33;
            {var subQ0=sQuery(id+"F19.wireOp",EDGE,"E52.MirrorC");var subQ1=sQuery(id+"F19.wireOp",EDGE,"E45");var subQ2=makeQuery(id+"F19.imprint","INTERSECT",VERTEX,{"disambiguationData":[OD(0.0)],"derivedFrom":[subQ1,subQ0]});Q33=makeQuery(id+"F19.imprint","IMPRINT",FACE,{"disambiguationData":[TD([[makeQuery(id+"F19.imprint","IMPRINT",EDGE,{"disambiguationData":[TD([[subQ2,-1.0]])],"derivedFrom":subQ1}),-1.0]])]});}
            var Q34;
            {var subQ0=sQuery(id+"F19.wireOp",EDGE,"E52.MirrorC");var subQ1=sQuery(id+"F19.wireOp",EDGE,"E45");var subQ2=makeQuery(id+"F19.imprint","INTERSECT",VERTEX,{"disambiguationData":[OD(0.0)],"derivedFrom":[subQ1,subQ0]});Q34=makeQuery(id+"F19.imprint","IMPRINT",FACE,{"disambiguationData":[TD([[makeQuery(id+"F19.imprint","IMPRINT",EDGE,{"disambiguationData":[TD([[subQ2,-1.0]])],"derivedFrom":subQ1}),1.0]])]});}
            extrude(context, id + "F20", {"entities" : qUnion([Q0, Q1, Q2, Q3, Q4, Q5, Q6, Q7, Q8, Q9, Q10, Q11, Q12, Q13, Q14, Q15, Q16, Q17, Q18, Q19, Q20, Q21, Q22, Q23, Q24, Q25, Q26, Q27, Q28, Q29, Q30, Q31, Q32, Q33, Q34]), "oppositeDirection" : true, "depth" : 4.5 * mm, "offsetDistance" : 25 * mm});
        }
    });
